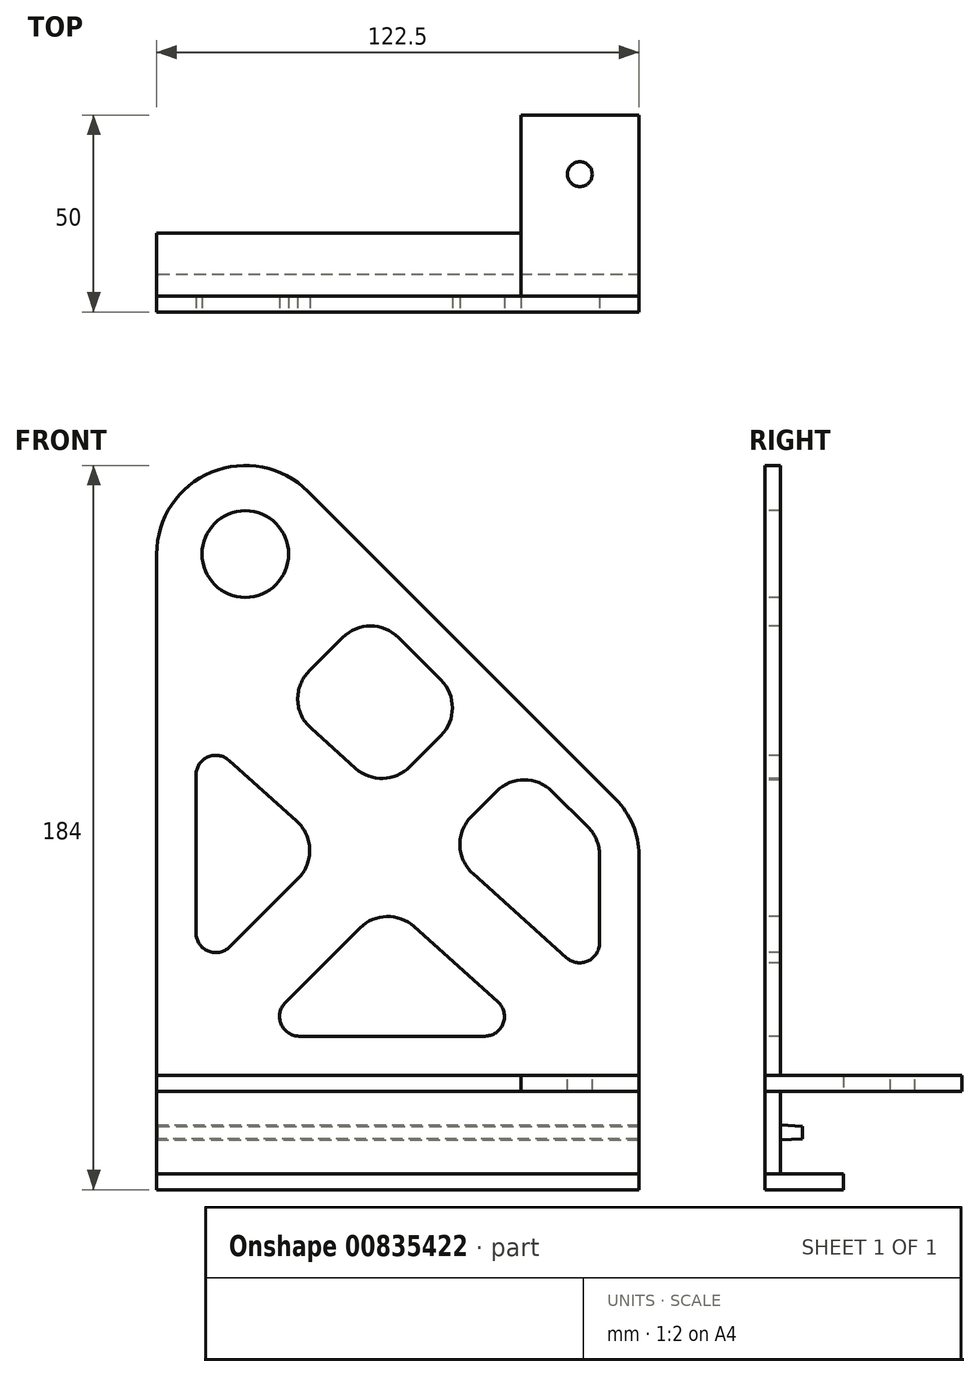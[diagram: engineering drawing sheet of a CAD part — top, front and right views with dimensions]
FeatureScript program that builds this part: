
annotation { "Feature Type Name" : "Feature", "Feature Type Description" : "" }
export const myFeature = defineFeature(function(context is Context, id is Id, definition is map)
    precondition{}
    {
        {
            var Q0;
            Q0=qCreatedBy(makeId("Front.planeOp"),FACE);
            var sketch = newSketch(context, id + "F0", { "sketchPlane" : qUnion([Q0])});
            skLineSegment(sketch, "E0.bottom", {"start": v(0, 0) * mm, "end": v(122.5, 0) * mm});
            skLineSegment(sketch, "E0.top", {"start": v(0, -4) * mm, "end": v(122.5, -4) * mm});
            skLineSegment(sketch, "E0.left", {"start": v(0, 0) * mm, "end": v(0, -4) * mm});
            skLineSegment(sketch, "E0.right", {"start": v(122.5, 0) * mm, "end": v(122.5, -4) * mm});
            skLineSegment(sketch, "E1.top", {"start": v(0, -25) * mm, "end": v(122.5, -25) * mm});
            skLineSegment(sketch, "E1.left", {"start": v(0, -4) * mm, "end": v(0, -25) * mm});
            skLineSegment(sketch, "E1.right", {"start": v(122.5, -4) * mm, "end": v(122.5, -25) * mm});
            skLineSegment(sketch, "E2", {"start": v(0, 110) * mm, "end": v(0, 132.5) * mm});
            skLineSegment(sketch, "E3", {"start": v(0, 132.5) * mm, "end": v(22.5, 132.5) * mm});
            skCircle(sketch, "E4", {"center": v(22.5, 132.5) * mm, "radius": 3.98 * mm});
            skCircle(sketch, "E5", {"center": v(22.5, 132.5) * mm, "radius": 11 * mm});
            skArc(sketch, "E6", {"start": v(38.4, 148.4) * mm, "mid": v(13.89, 153.29) * mm, "end": v(0, 132.5) * mm});
            skLineSegment(sketch, "E7", {"start": v(38.4, 148.4) * mm, "end": v(54.32, 132.5) * mm});
            skLineSegment(sketch, "E8", {"start": v(122.5, 0) * mm, "end": v(122.5, 56.04) * mm});
            skLineSegment(sketch, "E9", {"start": v(122.5, -25) * mm, "end": v(122.5, -29) * mm});
            skLineSegment(sketch, "E10", {"start": v(0, -12.6) * mm, "end": v(122.5, -12.6) * mm});
            skLineSegment(sketch, "E11", {"start": v(0, -16.4) * mm, "end": v(122.5, -16.4) * mm});
            skLineSegment(sketch, "E12", {"start": v(92.5, 0) * mm, "end": v(92.5, -4) * mm});
            skPoint(sketch, "E13.visualSharp", {"position": v(122.5, 64.32) * mm});
            skArc(sketch, "E13.filletArc", {"start": v(122.5, 56.04) * mm, "mid": v(120.98, 63.69) * mm, "end": v(116.64, 70.18) * mm});
            skPoint(sketch, "E14", {"position": v(57.96, 57.96) * mm});
            skLineSegment(sketch, "E15.trimOffspring", {"start": v(93.4, 93.4) * mm, "end": v(116.64, 70.18) * mm});
            skLineSegment(sketch, "E16", {"start": v(54.32, 132.5) * mm, "end": v(93.4, 93.4) * mm});
            skLineSegment(sketch, "E17", {"start": v(0, 110) * mm, "end": v(0, 0) * mm});
            skLineSegment(sketch, "E18.0", {"start": v(64.29, 78.43) * mm, "end": v(72.2, 86.34) * mm});
            skLineSegment(sketch, "E18.1", {"start": v(39.15, 88.29) * mm, "end": v(50.54, 78.06) * mm});
            skLineSegment(sketch, "E18.2", {"start": v(61.4, 111.29) * mm, "end": v(72.2, 100.48) * mm});
            skLineSegment(sketch, "E18.3", {"start": v(47.25, 111.29) * mm, "end": v(38.76, 102.8) * mm});
            skLineSegment(sketch, "E19.0", {"start": v(35.96, 50.1) * mm, "end": v(18.54, 32.68) * mm});
            skLineSegment(sketch, "E19.1", {"start": v(18.34, 80.1) * mm, "end": v(35.57, 64.62) * mm});
            skLineSegment(sketch, "E19.2", {"start": v(10, 76.37) * mm, "end": v(10, 36.21) * mm});
            skLineSegment(sketch, "E20.0", {"start": v(112.5, 33.63) * mm, "end": v(112.5, 56.04) * mm});
            skLineSegment(sketch, "E20.1", {"start": v(80.34, 51.3) * mm, "end": v(104.16, 29.9) * mm});
            skArc(sketch, "E20.2", {"start": v(112.5, 56.04) * mm, "mid": v(111.74, 59.86) * mm, "end": v(109.57, 63.1) * mm});
            skLineSegment(sketch, "E20.3", {"start": v(100.48, 72.2) * mm, "end": v(109.57, 63.1) * mm});
            skLineSegment(sketch, "E20.4", {"start": v(79.95, 65.8) * mm, "end": v(86.34, 72.2) * mm});
            skLineSegment(sketch, "E21.0", {"start": v(65.38, 37.85) * mm, "end": v(86.69, 18.72) * mm});
            skLineSegment(sketch, "E21.1", {"start": v(51.63, 37.48) * mm, "end": v(32.68, 18.54) * mm});
            skLineSegment(sketch, "E21.2", {"start": v(36.21, 10) * mm, "end": v(83.34, 10) * mm});
            skPoint(sketch, "E22.visualSharp", {"position": v(58.33, 44.18) * mm});
            skArc(sketch, "E22.filletArc", {"start": v(65.38, 37.85) * mm, "mid": v(58.43, 40.4) * mm, "end": v(51.63, 37.48) * mm});
            skPoint(sketch, "E23.visualSharp", {"position": v(24.14, 10) * mm});
            skArc(sketch, "E23.filletArc", {"start": v(32.68, 18.54) * mm, "mid": v(31.6, 13.09) * mm, "end": v(36.21, 10) * mm});
            skPoint(sketch, "E24.visualSharp", {"position": v(96.4, 10) * mm});
            skArc(sketch, "E24.filletArc", {"start": v(83.34, 10) * mm, "mid": v(88.01, 13.21) * mm, "end": v(86.69, 18.72) * mm});
            skPoint(sketch, "E25.visualSharp", {"position": v(112.5, 22.42) * mm});
            skArc(sketch, "E25.filletArc", {"start": v(104.16, 29.9) * mm, "mid": v(109.54, 29.06) * mm, "end": v(112.5, 33.63) * mm});
            skPoint(sketch, "E26.visualSharp", {"position": v(72.49, 58.35) * mm});
            skArc(sketch, "E26.filletArc", {"start": v(79.95, 65.8) * mm, "mid": v(77.03, 58.47) * mm, "end": v(80.34, 51.3) * mm});
            skPoint(sketch, "E27.visualSharp", {"position": v(57.59, 71.73) * mm});
            skArc(sketch, "E27.filletArc", {"start": v(50.54, 78.06) * mm, "mid": v(57.49, 75.5) * mm, "end": v(64.29, 78.43) * mm});
            skPoint(sketch, "E28.visualSharp", {"position": v(43.42, 57.57) * mm});
            skArc(sketch, "E28.filletArc", {"start": v(35.96, 50.1) * mm, "mid": v(38.89, 57.44) * mm, "end": v(35.57, 64.62) * mm});
            skPoint(sketch, "E29.visualSharp", {"position": v(93.4, 79.27) * mm});
            skArc(sketch, "E29.filletArc", {"start": v(100.48, 72.2) * mm, "mid": v(93.4, 75.13) * mm, "end": v(86.34, 72.2) * mm});
            skPoint(sketch, "E30.visualSharp", {"position": v(79.27, 93.4) * mm});
            skArc(sketch, "E30.filletArc", {"start": v(72.2, 86.34) * mm, "mid": v(75.13, 93.4) * mm, "end": v(72.2, 100.48) * mm});
            skPoint(sketch, "E31.visualSharp", {"position": v(10, 24.14) * mm});
            skArc(sketch, "E31.filletArc", {"start": v(10, 36.21) * mm, "mid": v(13.09, 31.6) * mm, "end": v(18.54, 32.68) * mm});
            skPoint(sketch, "E32.visualSharp", {"position": v(10, 87.58) * mm});
            skArc(sketch, "E32.filletArc", {"start": v(18.34, 80.1) * mm, "mid": v(12.96, 80.94) * mm, "end": v(10, 76.37) * mm});
            skPoint(sketch, "E33.visualSharp", {"position": v(54.32, 118.36) * mm});
            skArc(sketch, "E33.filletArc", {"start": v(61.4, 111.29) * mm, "mid": v(54.32, 114.22) * mm, "end": v(47.25, 111.29) * mm});
            skPoint(sketch, "E34.start.orphan", {"position": v(22.5, 110) * mm});
            skPoint(sketch, "E35.visualSharp", {"position": v(31.3, 95.34) * mm});
            skArc(sketch, "E35.filletArc", {"start": v(38.76, 102.8) * mm, "mid": v(35.83, 95.46) * mm, "end": v(39.15, 88.29) * mm});
            skLineSegment(sketch, "E36", {"start": v(0, -29) * mm, "end": v(0, -25) * mm});
            skLineSegment(sketch, "E37", {"start": v(122.5, -29) * mm, "end": v(0, -29) * mm});
            skSolve(sketch);
        }
        {
            var Q0;
            {var subQ0=sQuery(id+"F0.wireOp",EDGE,"E2");Q0=makeQuery(id+"F0.imprint","IMPRINT",FACE,{"disambiguationData":[TD([[makeQuery(id+"F0.imprint","IMPRINT",EDGE,{"derivedFrom":subQ0}),-1.0]])]});}
            var Q1;
            {var subQ3=sQuery(id+"F0.wireOp",EDGE,"E10");Q1=makeQuery(id+"F0.imprint","IMPRINT",FACE,{"disambiguationData":[TD([[makeQuery(id+"F0.imprint","IMPRINT",EDGE,{"derivedFrom":subQ3}),1.0]])]});}
            var Q2;
            {var subQ3=sQuery(id+"F0.wireOp",EDGE,"E11");Q2=makeQuery(id+"F0.imprint","IMPRINT",FACE,{"disambiguationData":[TD([[makeQuery(id+"F0.imprint","IMPRINT",EDGE,{"derivedFrom":subQ3}),-1.0]])]});}
            extrude(context, id + "F1", {"entities" : qUnion([Q0, Q1, Q2]), "depth" : 4 * mm, "offsetDistance" : 25 * mm});
        }
        {
            var Q0;
            {var subQ0=sQuery(id+"F0.wireOp",EDGE,"E0.left");Q0=makeQuery(id+"F0.imprint","IMPRINT",FACE,{"disambiguationData":[TD([[makeQuery(id+"F0.imprint","IMPRINT",EDGE,{"derivedFrom":subQ0}),1.0]])]});}
            var Q1;
            Q1=makeQuery(id+"F0.imprint","IMPRINT",FACE,{"disambiguationData":[TD([[makeQuery(id+"F0.imprint","IMPRINT",EDGE,{"derivedFrom":sQuery(id+"F0.wireOp",EDGE,"E1.top")}),-1.0]])]});
            extrude(context, id + "F2", {"entities" : qUnion([Q0, Q1]), "depth" : 20 * mm, "offsetDistance" : 25 * mm});
        }
        {
            var Q0;
            {var subQ0=sQuery(id+"F0.wireOp",EDGE,"E0.right");Q0=makeQuery(id+"F0.imprint","IMPRINT",FACE,{"disambiguationData":[TD([[makeQuery(id+"F0.imprint","IMPRINT",EDGE,{"derivedFrom":subQ0}),-1.0]])]});}
            extrude(context, id + "F3", {"entities" : qUnion([Q0]), "depth" : 50 * mm, "offsetDistance" : 25 * mm});
        }
        {
            var Q0;
            {var subQ0=sQuery(id+"F0.wireOp",EDGE,"E10");Q0=makeQuery(id+"F0.imprint","IMPRINT",FACE,{"disambiguationData":[TD([[makeQuery(id+"F0.imprint","IMPRINT",EDGE,{"derivedFrom":subQ0}),-1.0]])]});}
            extrude(context, id + "F4", {"entities" : qUnion([Q0]), "depth" : 4 * mm, "offsetDistance" : 25 * mm});
        }
        {
            var Q0;
            Q0=makeQuery(id+"F3.opExtrude","SWEPT_FACE",FACE,{"disambiguationData":[OSD([sQuery(id+"F0.wireOp",EDGE,"E0.bottom")])]});
            var sketch = newSketch(context, id + "F5", { "sketchPlane" : qUnion([Q0])});
            skCircle(sketch, "E38", {"center": v(107.5, -35) * mm, "radius": 3.15 * mm});
            skSolve(sketch);
        }
        {
            var Q0;
            Q0=makeQuery(id+"F5.imprint","IMPRINT",FACE,{"disambiguationData":[TD([[makeQuery(id+"F5.imprint","IMPRINT",EDGE,{"derivedFrom":sQuery(id+"F5.wireOp",EDGE,"E38")}),1.0]])]});
            extrude(context, id + "F6", {"entities" : qUnion([Q0]), "operationType" : NewBodyOperationType.REMOVE, "oppositeDirection" : true, "depth" : 40 * mm, "offsetDistance" : 25 * mm});
        }
        {
            var Q0;
            Q0=makeQuery(id+"F4.opExtrude","CAP_FACE",FACE,{"disambiguationData":[OSD([sQuery(id+"F0.wireOp",EDGE,"E1.left"),sQuery(id+"F0.wireOp",EDGE,"E1.right"),sQuery(id+"F0.wireOp",EDGE,"E10"),sQuery(id+"F0.wireOp",EDGE,"E11")])],"isStart":false});
            extrude(context, id + "F7", {"entities" : qUnion([Q0]), "operationType" : NewBodyOperationType.ADD, "depth" : 5.6 * mm, "offsetDistance" : 25 * mm, "hasDraft" : true, "draftAngle" : 3 * degree, "draftPullDirection" : true});
        }
        {
            var Q0;
            Q0=makeQuery(id+"F4.opExtrude","SWEPT_BODY",BODY,{"disambiguationData":[OSD([sQuery(id+"F0.wireOp",EDGE,"E1.left"),sQuery(id+"F0.wireOp",EDGE,"E1.right"),sQuery(id+"F0.wireOp",EDGE,"E10"),sQuery(id+"F0.wireOp",EDGE,"E11")])]});
            var Q1;
            Q1=makeQuery(id+"F1.opExtrude","SWEPT_BODY",BODY,{"disambiguationData":[OSD([sQuery(id+"F0.wireOp",EDGE,"E0.bottom"),sQuery(id+"F0.wireOp",EDGE,"E2"),sQuery(id+"F0.wireOp",EDGE,"E5"),sQuery(id+"F0.wireOp",EDGE,"E7"),sQuery(id+"F0.wireOp",EDGE,"E8"),sQuery(id+"F0.wireOp",EDGE,"E13.filletArc"),sQuery(id+"F0.wireOp",EDGE,"E6"),sQuery(id+"F0.wireOp",EDGE,"E15.trimOffspring"),sQuery(id+"F0.wireOp",EDGE,"E16"),sQuery(id+"F0.wireOp",EDGE,"E17"),sQuery(id+"F0.wireOp",EDGE,"E18.0"),sQuery(id+"F0.wireOp",EDGE,"E18.1"),sQuery(id+"F0.wireOp",EDGE,"E18.2"),sQuery(id+"F0.wireOp",EDGE,"E18.3"),sQuery(id+"F0.wireOp",EDGE,"E19.0"),sQuery(id+"F0.wireOp",EDGE,"E19.1"),sQuery(id+"F0.wireOp",EDGE,"E19.2"),sQuery(id+"F0.wireOp",EDGE,"E20.0"),sQuery(id+"F0.wireOp",EDGE,"E20.1"),sQuery(id+"F0.wireOp",EDGE,"E20.2"),sQuery(id+"F0.wireOp",EDGE,"E20.3"),sQuery(id+"F0.wireOp",EDGE,"E20.4"),sQuery(id+"F0.wireOp",EDGE,"E21.0"),sQuery(id+"F0.wireOp",EDGE,"E21.1"),sQuery(id+"F0.wireOp",EDGE,"E21.2"),sQuery(id+"F0.wireOp",EDGE,"E22.filletArc"),sQuery(id+"F0.wireOp",EDGE,"E23.filletArc"),sQuery(id+"F0.wireOp",EDGE,"E24.filletArc"),sQuery(id+"F0.wireOp",EDGE,"E25.filletArc"),sQuery(id+"F0.wireOp",EDGE,"E26.filletArc"),sQuery(id+"F0.wireOp",EDGE,"E27.filletArc"),sQuery(id+"F0.wireOp",EDGE,"E28.filletArc"),sQuery(id+"F0.wireOp",EDGE,"E29.filletArc"),sQuery(id+"F0.wireOp",EDGE,"E30.filletArc"),sQuery(id+"F0.wireOp",EDGE,"E31.filletArc"),sQuery(id+"F0.wireOp",EDGE,"E32.filletArc"),sQuery(id+"F0.wireOp",EDGE,"E33.filletArc"),sQuery(id+"F0.wireOp",EDGE,"E35.filletArc")])]});
            var Q2;
            Q2=makeQuery(id+"F1.opExtrude","SWEPT_BODY",BODY,{"disambiguationData":[OSD([sQuery(id+"F0.wireOp",EDGE,"E1.top"),sQuery(id+"F0.wireOp",EDGE,"E1.left"),sQuery(id+"F0.wireOp",EDGE,"E1.right"),sQuery(id+"F0.wireOp",EDGE,"E11")])]});
            var Q3;
            Q3=makeQuery(id+"F2.opExtrude","SWEPT_BODY",BODY,{"disambiguationData":[OSD([sQuery(id+"F0.wireOp",EDGE,"E0.bottom"),sQuery(id+"F0.wireOp",EDGE,"E0.left"),sQuery(id+"F0.wireOp",EDGE,"E0.top"),sQuery(id+"F0.wireOp",EDGE,"E12")])]});
            var Q4;
            Q4=makeQuery(id+"F3.opExtrude","SWEPT_BODY",BODY,{"disambiguationData":[OSD([sQuery(id+"F0.wireOp",EDGE,"E0.bottom"),sQuery(id+"F0.wireOp",EDGE,"E0.right"),sQuery(id+"F0.wireOp",EDGE,"E0.top"),sQuery(id+"F0.wireOp",EDGE,"E12")])]});
            var Q5;
            Q5=makeQuery(id+"F1.opExtrude","SWEPT_BODY",BODY,{"disambiguationData":[OSD([sQuery(id+"F0.wireOp",EDGE,"E0.top"),sQuery(id+"F0.wireOp",EDGE,"E1.left"),sQuery(id+"F0.wireOp",EDGE,"E1.right"),sQuery(id+"F0.wireOp",EDGE,"E10")])]});
            var Q6;
            Q6=makeQuery(id+"F2.opExtrude","SWEPT_BODY",BODY,{"disambiguationData":[OSD([sQuery(id+"F0.wireOp",EDGE,"E1.top"),sQuery(id+"F0.wireOp",EDGE,"E9"),sQuery(id+"F0.wireOp",EDGE,"E36"),sQuery(id+"F0.wireOp",EDGE,"E37")])]});
            var Q7;
            Q7=qCreatedBy(makeId("Front.planeOp"),FACE);
            mirror(context, id + "F8", {"entities" : qUnion([Q0, Q1, Q2, Q3, Q4, Q5, Q6]), "mirrorPlane" : qUnion([Q7])});
        }
        {
            var Q0;
            Q0=makeQuery(id+"F1.opExtrude","SWEPT_BODY",BODY,{"disambiguationData":[OSD([sQuery(id+"F0.wireOp",EDGE,"E0.bottom"),sQuery(id+"F0.wireOp",EDGE,"E2"),sQuery(id+"F0.wireOp",EDGE,"E5"),sQuery(id+"F0.wireOp",EDGE,"E7"),sQuery(id+"F0.wireOp",EDGE,"E8"),sQuery(id+"F0.wireOp",EDGE,"E13.filletArc"),sQuery(id+"F0.wireOp",EDGE,"E6"),sQuery(id+"F0.wireOp",EDGE,"E15.trimOffspring"),sQuery(id+"F0.wireOp",EDGE,"E16"),sQuery(id+"F0.wireOp",EDGE,"E17"),sQuery(id+"F0.wireOp",EDGE,"E18.0"),sQuery(id+"F0.wireOp",EDGE,"E18.1"),sQuery(id+"F0.wireOp",EDGE,"E18.2"),sQuery(id+"F0.wireOp",EDGE,"E18.3"),sQuery(id+"F0.wireOp",EDGE,"E19.0"),sQuery(id+"F0.wireOp",EDGE,"E19.1"),sQuery(id+"F0.wireOp",EDGE,"E19.2"),sQuery(id+"F0.wireOp",EDGE,"E20.0"),sQuery(id+"F0.wireOp",EDGE,"E20.1"),sQuery(id+"F0.wireOp",EDGE,"E20.2"),sQuery(id+"F0.wireOp",EDGE,"E20.3"),sQuery(id+"F0.wireOp",EDGE,"E20.4"),sQuery(id+"F0.wireOp",EDGE,"E21.0"),sQuery(id+"F0.wireOp",EDGE,"E21.1"),sQuery(id+"F0.wireOp",EDGE,"E21.2"),sQuery(id+"F0.wireOp",EDGE,"E22.filletArc"),sQuery(id+"F0.wireOp",EDGE,"E23.filletArc"),sQuery(id+"F0.wireOp",EDGE,"E24.filletArc"),sQuery(id+"F0.wireOp",EDGE,"E25.filletArc"),sQuery(id+"F0.wireOp",EDGE,"E26.filletArc"),sQuery(id+"F0.wireOp",EDGE,"E27.filletArc"),sQuery(id+"F0.wireOp",EDGE,"E28.filletArc"),sQuery(id+"F0.wireOp",EDGE,"E29.filletArc"),sQuery(id+"F0.wireOp",EDGE,"E30.filletArc"),sQuery(id+"F0.wireOp",EDGE,"E31.filletArc"),sQuery(id+"F0.wireOp",EDGE,"E32.filletArc"),sQuery(id+"F0.wireOp",EDGE,"E33.filletArc"),sQuery(id+"F0.wireOp",EDGE,"E35.filletArc")])]});
            var Q1;
            Q1=makeQuery(id+"F2.opExtrude","SWEPT_BODY",BODY,{"disambiguationData":[OSD([sQuery(id+"F0.wireOp",EDGE,"E0.bottom"),sQuery(id+"F0.wireOp",EDGE,"E0.left"),sQuery(id+"F0.wireOp",EDGE,"E0.top"),sQuery(id+"F0.wireOp",EDGE,"E12")])]});
            var Q2;
            Q2=makeQuery(id+"F3.opExtrude","SWEPT_BODY",BODY,{"disambiguationData":[OSD([sQuery(id+"F0.wireOp",EDGE,"E0.bottom"),sQuery(id+"F0.wireOp",EDGE,"E0.right"),sQuery(id+"F0.wireOp",EDGE,"E0.top"),sQuery(id+"F0.wireOp",EDGE,"E12")])]});
            var Q3;
            Q3=makeQuery(id+"F2.opExtrude","SWEPT_BODY",BODY,{"disambiguationData":[OSD([sQuery(id+"F0.wireOp",EDGE,"E1.top"),sQuery(id+"F0.wireOp",EDGE,"E9"),sQuery(id+"F0.wireOp",EDGE,"E36"),sQuery(id+"F0.wireOp",EDGE,"E37")])]});
            var Q4;
            Q4=makeQuery(id+"F1.opExtrude","SWEPT_BODY",BODY,{"disambiguationData":[OSD([sQuery(id+"F0.wireOp",EDGE,"E0.top"),sQuery(id+"F0.wireOp",EDGE,"E1.left"),sQuery(id+"F0.wireOp",EDGE,"E1.right"),sQuery(id+"F0.wireOp",EDGE,"E10")])]});
            var Q5;
            Q5=makeQuery(id+"F4.opExtrude","SWEPT_BODY",BODY,{"disambiguationData":[OSD([sQuery(id+"F0.wireOp",EDGE,"E1.left"),sQuery(id+"F0.wireOp",EDGE,"E1.right"),sQuery(id+"F0.wireOp",EDGE,"E10"),sQuery(id+"F0.wireOp",EDGE,"E11")])]});
            var Q6;
            Q6=makeQuery(id+"F1.opExtrude","SWEPT_BODY",BODY,{"disambiguationData":[OSD([sQuery(id+"F0.wireOp",EDGE,"E1.top"),sQuery(id+"F0.wireOp",EDGE,"E1.left"),sQuery(id+"F0.wireOp",EDGE,"E1.right"),sQuery(id+"F0.wireOp",EDGE,"E11")])]});
            deleteBodies(context, id + "F9", {"entities" : qUnion([Q0, Q1, Q2, Q3, Q4, Q5, Q6])});
        }
    });
